# Revit family: DAISY COMBO
name_source: partatom
category: Furniture Systems
units: mm (PartAtom-declared; Revit-internal decimal feet)

## family parameters
Always vertical = Yes
Cut with Voids When Loaded = No
Part Type = Normal
Room Calculation Point = No
Round Connector Dimension = Use Diameter
Shared = No
Work Plane-Based = No

## types (1)
- DAISY COMBO
    30" Round Ottoman = F005-30x18
    30" Round Ottoman Seat Fabric = <By Category>
    30" Round Ottoman Side Fabric = <By Category>
    Base = <By Category>
    Description = Combo Products - DAISY COMBO
    Glide = <By Category>
    Manufacturer = FOMCORE
    Model = DAISY COMBO
    Petal Ottoman = F101-18x18
    Petal Ottoman-Seat fabric-1 = <By Category>
    Petal Ottoman-Seat fabric-2 = <By Category>
    Petal Ottoman-Seat fabric-3 = <By Category>
    Petal Ottoman-Seat fabric-4 = <By Category>
    Petal Ottoman-Seat fabric-5 = <By Category>
    Petal Ottoman-Seat fabric-6 = <By Category>
    Petal Ottoman-Side fabric-1 = <By Category>
    Petal Ottoman-Side fabric-2 = <By Category>
    Petal Ottoman-Side fabric-3 = <By Category>
    Petal Ottoman-Side fabric-4 = <By Category>
    Petal Ottoman-Side fabric-5 = <By Category>
    Petal Ottoman-Side fabric-6 = <By Category>
    URL = https://fomcore.com

## geometry (parser evidence)
native form markers: Sweep x2
no freeform markers — native parametric forms only
